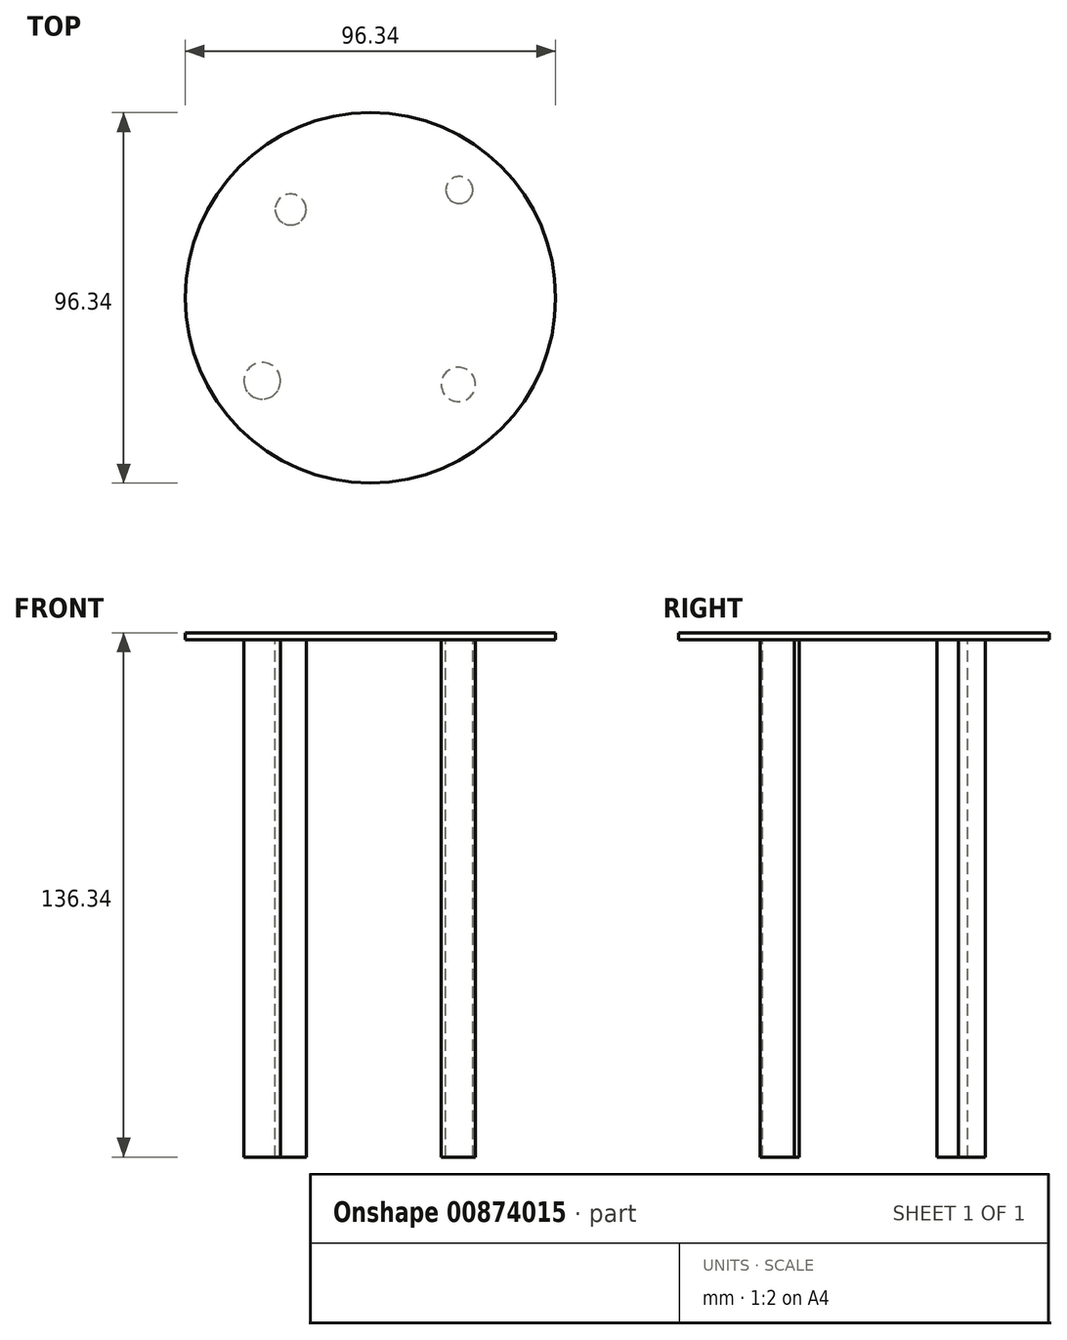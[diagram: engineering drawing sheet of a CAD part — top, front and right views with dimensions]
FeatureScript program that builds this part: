
annotation { "Feature Type Name" : "Feature", "Feature Type Description" : "" }
export const myFeature = defineFeature(function(context is Context, id is Id, definition is map)
    precondition{}
    {
        {
            var Q0;
            Q0=qCreatedBy(makeId("Top.planeOp"),FACE);
            var sketch = newSketch(context, id + "F0", { "sketchPlane" : qUnion([Q0])});
            skCircle(sketch, "E0", {"center": v(0, 0) * mm, "radius": 52.1 * mm});
            skCircle(sketch, "E1", {"center": v(0, 0) * mm, "radius": 48.17 * mm});
            skSolve(sketch);
        }
        {
            var Q0;
            Q0=makeQuery(id+"F0.imprint","IMPRINT",FACE,{"disambiguationData":[TD([[makeQuery(id+"F0.imprint","IMPRINT",EDGE,{"derivedFrom":sQuery(id+"F0.wireOp",EDGE,"E1")}),1.0]])]});
            extrude(context, id + "F1", {"entities" : qUnion([Q0]), "depth" : 1.75 * mm, "offsetDistance" : 25.4 * mm});
        }
        {
            var Q0;
            Q0=makeQuery(id+"F1.opExtrude","CAP_FACE",FACE,{"disambiguationData":[OSD([sQuery(id+"F0.wireOp",EDGE,"E1")])],"isStart":true});
            var sketch = newSketch(context, id + "F2", { "sketchPlane" : qUnion([Q0])});
            skSolve(sketch);
        }
        {
            var Q0;
            Q0=makeQuery(id+"F2.imprint","IMPRINT",FACE,{"disambiguationData":[TD([[makeQuery(id+"F2.imprint","IMPRINT",EDGE,{"derivedFrom":makeQuery(id+"F1.opExtrude","CAP_EDGE",EDGE,{"disambiguationData":[OSD([sQuery(id+"F0.wireOp",EDGE,"E1")])],"isStart":true})}),-1.0]])]});
            var sketch = newSketch(context, id + "F3", { "sketchPlane" : qUnion([Q0])});
            skCircle(sketch, "E2", {"center": v(22.85, 22.53) * mm, "radius": 4.45 * mm});
            skCircle(sketch, "E3", {"center": v(23.1, -28.07) * mm, "radius": 3.52 * mm});
            skCircle(sketch, "E4", {"center": v(-20.74, -22.99) * mm, "radius": 4.02 * mm});
            skCircle(sketch, "E5", {"center": v(-28.15, 21.58) * mm, "radius": 4.77 * mm});
            skSolve(sketch);
        }
        {
            var Q0;
            Q0=makeQuery(id+"F3.imprint","IMPRINT",FACE,{"disambiguationData":[TD([[makeQuery(id+"F3.imprint","IMPRINT",EDGE,{"derivedFrom":sQuery(id+"F3.wireOp",EDGE,"E4")}),1.0]])]});
            var Q1;
            Q1=makeQuery(id+"F3.imprint","IMPRINT",FACE,{"disambiguationData":[TD([[makeQuery(id+"F3.imprint","IMPRINT",EDGE,{"derivedFrom":sQuery(id+"F3.wireOp",EDGE,"E5")}),1.0]])]});
            var Q2;
            Q2=makeQuery(id+"F3.imprint","IMPRINT",FACE,{"disambiguationData":[TD([[makeQuery(id+"F3.imprint","IMPRINT",EDGE,{"derivedFrom":sQuery(id+"F3.wireOp",EDGE,"E2")}),1.0]])]});
            var Q3;
            Q3=makeQuery(id+"F3.imprint","IMPRINT",FACE,{"disambiguationData":[TD([[makeQuery(id+"F3.imprint","IMPRINT",EDGE,{"derivedFrom":sQuery(id+"F3.wireOp",EDGE,"E3")}),1.0]])]});
            extrude(context, id + "F4", {"entities" : qUnion([Q0, Q1, Q2, Q3]), "operationType" : NewBodyOperationType.ADD, "depth" : 134.6 * mm, "offsetDistance" : 25.4 * mm});
        }
    });
